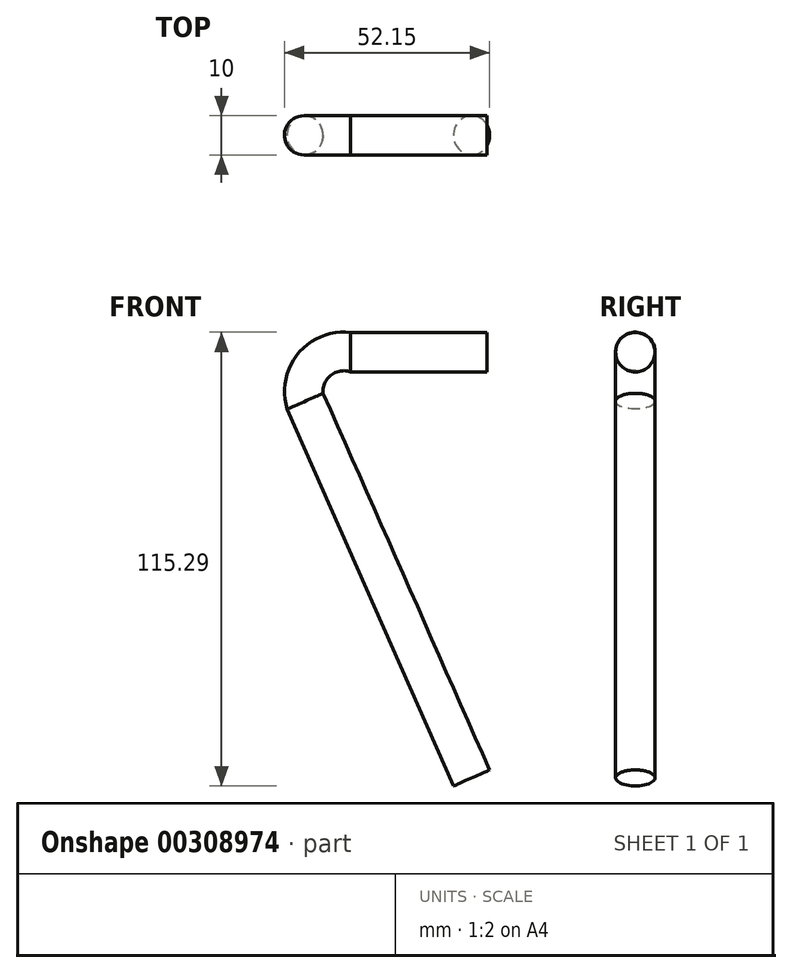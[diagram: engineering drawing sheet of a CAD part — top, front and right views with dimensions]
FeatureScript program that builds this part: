
annotation { "Feature Type Name" : "Feature", "Feature Type Description" : "" }
export const myFeature = defineFeature(function(context is Context, id is Id, definition is map)
    precondition{}
    {
        {
            var Q0;
            Q0=qCreatedBy(makeId("Front.planeOp"),FACE);
            var sketch = newSketch(context, id + "F0", { "sketchPlane" : qUnion([Q0])});
            skLineSegment(sketch, "E0", {"start": v(-45.52, 27.86) * mm, "end": v(-3.2, -67.84) * mm});
            skLineSegment(sketch, "E1", {"start": v(-36.37, 41.9) * mm, "end": v(-1.73, 41.9) * mm});
            skPoint(sketch, "E2.visualSharp", {"position": v(-51.73, 41.9) * mm});
            skArc(sketch, "E2.filletArc", {"start": v(-36.37, 41.9) * mm, "mid": v(-44.75, 37.36) * mm, "end": v(-45.52, 27.86) * mm});
            skSolve(sketch);
        }
        {
            var Q0;
            Q0=qCreatedBy(makeId("Right.planeOp"),FACE);
            var sketch = newSketch(context, id + "F1", { "sketchPlane" : qUnion([Q0])});
            skCircle(sketch, "E3", {"center": v(0, 41.9) * mm, "radius": 5 * mm});
            skSolve(sketch);
        }
        {
            var Q0;
            Q0=makeQuery(id+"F1.imprint","IMPRINT",FACE,{"disambiguationData":[TD([[makeQuery(id+"F1.imprint","IMPRINT",EDGE,{"derivedFrom":sQuery(id+"F1.wireOp",EDGE,"E3")}),1.0]])]});
            var Q1;
            Q1=sQuery(id+"F0.wireOp",EDGE,"E1");
            var Q2;
            Q2=sQuery(id+"F0.wireOp",EDGE,"E2.filletArc");
            var Q3;
            Q3=sQuery(id+"F0.wireOp",EDGE,"E0");
            sweep(context, id + "F2", {"profiles" : qUnion([Q0]), "path" : qUnion([Q1, Q2, Q3])});
        }
    });
